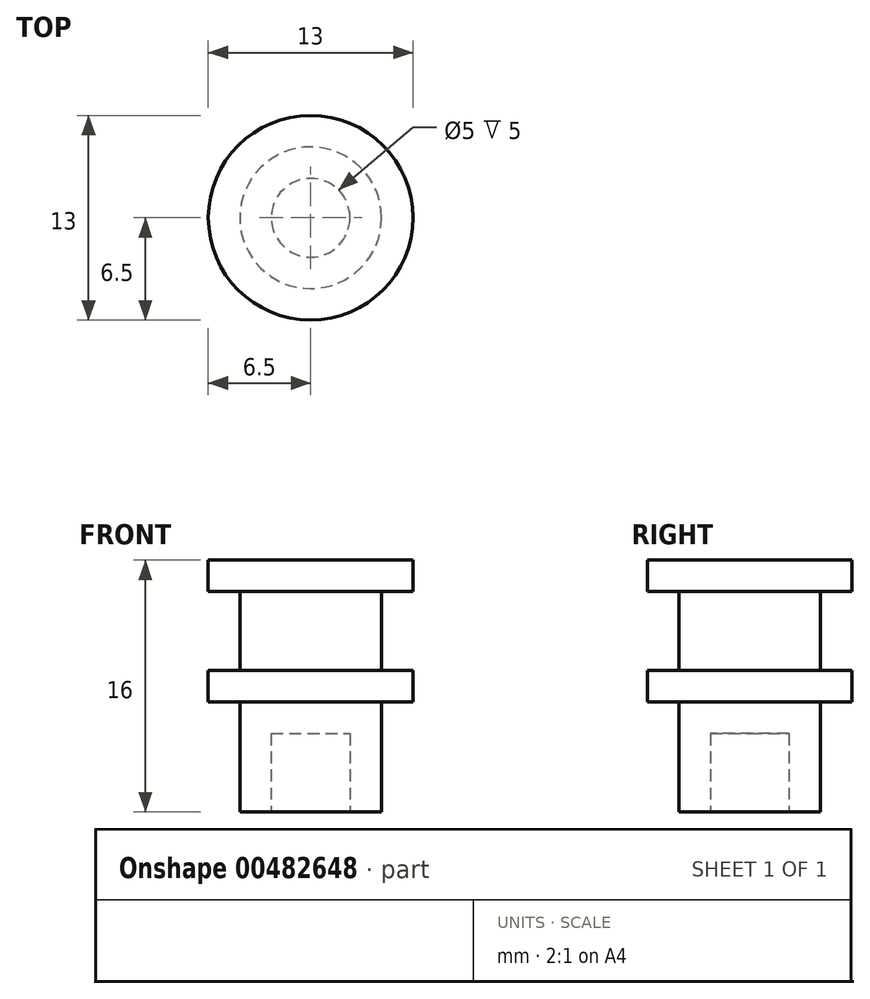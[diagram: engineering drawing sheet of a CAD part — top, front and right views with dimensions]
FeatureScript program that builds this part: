
annotation { "Feature Type Name" : "Feature", "Feature Type Description" : "" }
export const myFeature = defineFeature(function(context is Context, id is Id, definition is map)
    precondition{}
    {
        {
            var Q0;
            Q0=qCreatedBy(makeId("Front.planeOp"),FACE);
            var sketch = newSketch(context, id + "F0", { "sketchPlane" : qUnion([Q0])});
            skLineSegment(sketch, "E0", {"start": v(0, 0) * mm, "end": v(0, 9) * mm});
            skLineSegment(sketch, "E1", {"start": v(0, 9) * mm, "end": v(-6.5, 9) * mm});
            skLineSegment(sketch, "E2", {"start": v(-6.5, 9) * mm, "end": v(-6.5, 7) * mm});
            skLineSegment(sketch, "E3", {"start": v(-6.5, 7) * mm, "end": v(-4.5, 7) * mm});
            skLineSegment(sketch, "E4", {"start": v(-4.5, 7) * mm, "end": v(-4.5, 2) * mm});
            skLineSegment(sketch, "E5", {"start": v(-4.5, 2) * mm, "end": v(-6.5, 2) * mm});
            skLineSegment(sketch, "E6", {"start": v(-6.5, 2) * mm, "end": v(-6.5, 0) * mm});
            skLineSegment(sketch, "E7", {"start": v(-6.5, 0) * mm, "end": v(-4.5, 0) * mm});
            skLineSegment(sketch, "E8", {"start": v(-4.5, 0) * mm, "end": v(-4.5, -7) * mm});
            skLineSegment(sketch, "E9", {"start": v(-4.5, -7) * mm, "end": v(-2.5, -7) * mm});
            skLineSegment(sketch, "E10", {"start": v(-2.5, -7) * mm, "end": v(-2.5, -2) * mm});
            skLineSegment(sketch, "E11", {"start": v(-2.5, -2) * mm, "end": v(0, -2) * mm});
            skLineSegment(sketch, "E12", {"start": v(0, -2) * mm, "end": v(0, 0) * mm});
            skLineSegment(sketch, "E13", {"start": v(-0.44, 0) * mm, "end": v(-0.44, -2) * mm, "construction": true});
            skLineSegment(sketch, "E14", {"start": v(-4.5, 4.5) * mm, "end": v(0, 4.5) * mm, "construction": true});
            skSolve(sketch);
        }
        {
            var Q0;
            Q0=makeQuery(id+"F0.imprint","IMPRINT",FACE,{"disambiguationData":[TD([[makeQuery(id+"F0.imprint","IMPRINT",EDGE,{"derivedFrom":sQuery(id+"F0.wireOp",EDGE,"E0")}),1.0]])]});
            var Q1;
            Q1=sQuery(id+"F0.wireOp",EDGE,"E0");
            revolve(context, id + "F1", {"entities" : qUnion([Q0]), "axis" : qUnion([Q1]), "revolveType" : RevolveType.FULL});
        }
    });
